# Revit family: DSI-H_3HR_Horizontal_Curtain_Under_Ceiling
name_source: partatom
category: Specialty Equipment
units: mm (PartAtom-declared; Revit-internal decimal feet)

## family parameters
Always vertical = Yes
Cut with Voids When Loaded = No
Enable Cutting in Views = No
Maintain Annotation Orientation = No
OmniClass Number = 23.30.60.17
OmniClass Title = Fire and Smoke Shutters and Curtains
Part Type = Normal
Room Calculation Point = No
Round Connector Dimension = Use Diameter
Shared = No
Work Plane-Based = No

## types (1)
- DSI-H_3HR_Horizontal_Curtain_Under_Ceiling
    Bottom Bar = 2mm THK  GALVANIZED STEEL  BOTTOM BAR
    Cost = 0 $
    Curtain = Curtain
    Curtain Box = 1.2mmTHK GALVANISED STEEL
    Curtain Fabric = MANUFACTURED FROM STAINLESS STEEL, WIRE REINFORCED,
WOVEN GLASS FIBRE, FABRIC COATED ON EACH SIDE
WITH SILVER POLYURETHANE  VWG 690
    Default Elevation = 0' - 0"
    End Plate = 3mmTHK GALVANISED STEEL END PLATES AND BRACKETS
    Galvanized Stell = Galvanized Steel
    Guide Rail = 2 mm THK GALVANIZED STEEL GUIDE RAIL
    Manufacturer = Door Systems
    Model = DSI-H 3HR HorizontalnCurtain Under Ceiling
    Motor = INTERNAL, ELECTRIC, TUBULER GEARED CONSTANT SPEED MOTOR
    Open Fire Curtain = Yes
    Power Supply = SINGLE PHASE, 230V,13A,50Hz
    Product Information = https://www.arcat.com
    Schematic Floor = No
    Specifications = https://www.arcat.com
    Stainless Steel = Stainless Steel
    URL = https://www.doorsysinc.com

## geometry (parser evidence)
native form markers: Sweep x3
no freeform markers — native parametric forms only
